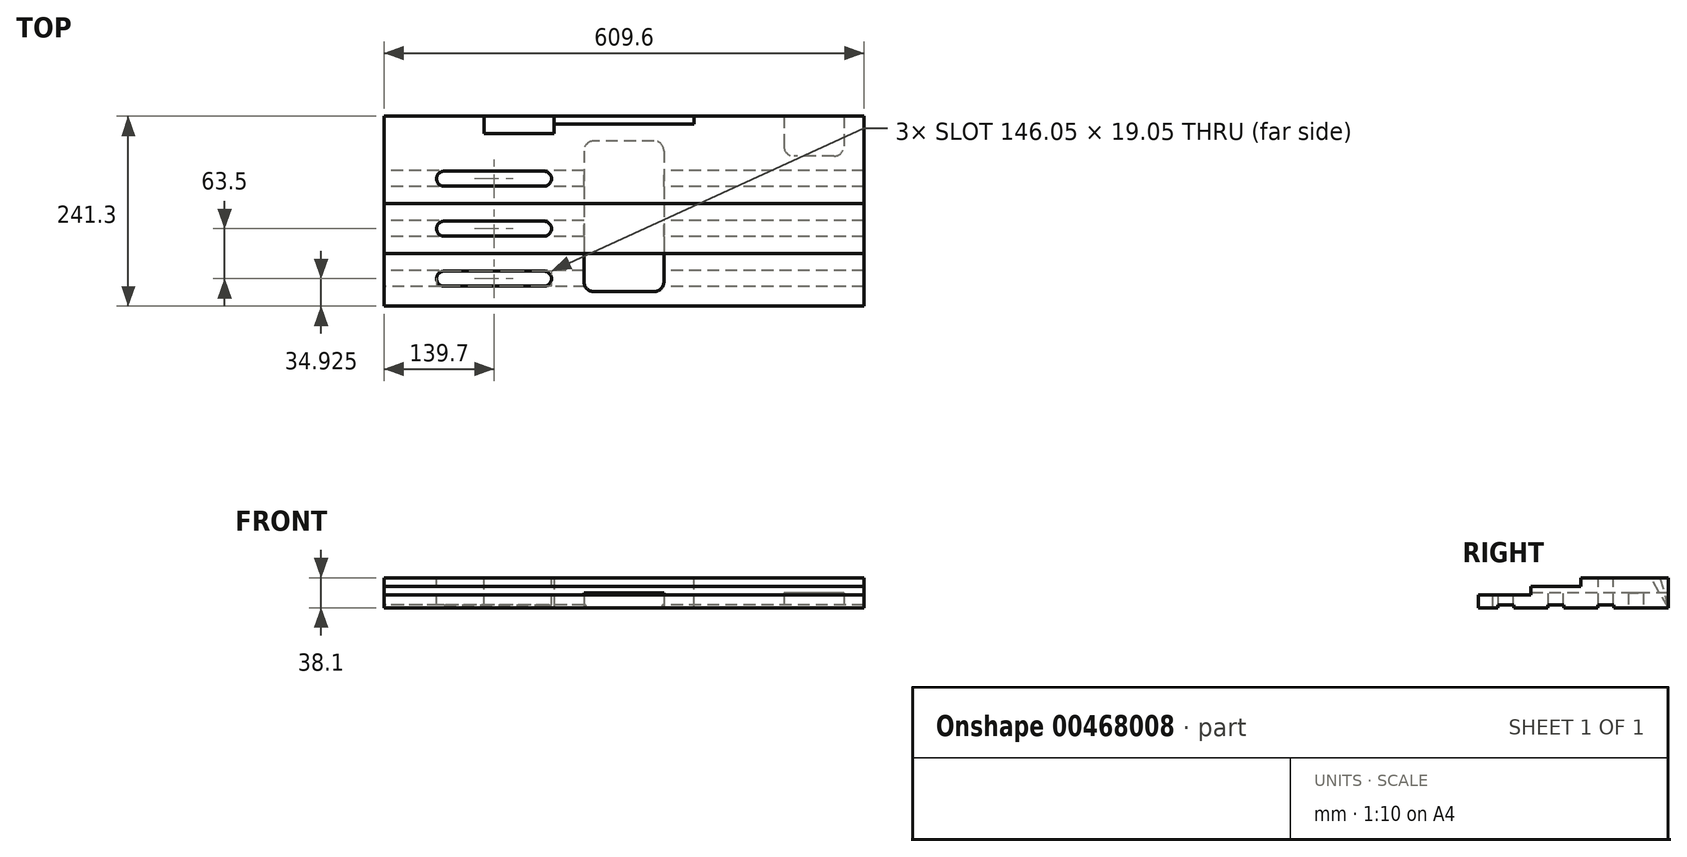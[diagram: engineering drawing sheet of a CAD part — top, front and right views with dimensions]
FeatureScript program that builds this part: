
annotation { "Feature Type Name" : "Feature", "Feature Type Description" : "" }
export const myFeature = defineFeature(function(context is Context, id is Id, definition is map)
    precondition{}
    {
        {
            var Q0;
            Q0=qCreatedBy(makeId("Top.planeOp"),FACE);
            var sketch = newSketch(context, id + "F0", { "sketchPlane" : qUnion([Q0])});
            skLineSegment(sketch, "E0.bottom", {"start": v(304.8, 120.65) * mm, "end": v(-304.8, 120.65) * mm});
            skLineSegment(sketch, "E0.top", {"start": v(304.8, -120.65) * mm, "end": v(-304.8, -120.65) * mm});
            skLineSegment(sketch, "E0.left", {"start": v(304.8, 120.65) * mm, "end": v(304.8, -120.65) * mm});
            skLineSegment(sketch, "E0.right", {"start": v(-304.8, 120.65) * mm, "end": v(-304.8, -120.65) * mm});
            skPoint(sketch, "E0.middle", {"position": v(0, 0) * mm});
            skSolve(sketch);
        }
        {
            var Q0;
            Q0 = qSketchRegion(id + "F0", true);
            extrude(context, id + "F1", {"entities" : qUnion([Q0]), "depth" : 38.1 * mm});
        }
        {
            var Q0;
            Q0=makeQuery(id+"F1.opExtrude","CAP_FACE",FACE,{"disambiguationData":[OSD([sQuery(id+"F0.wireOp",EDGE,"E0.bottom"),sQuery(id+"F0.wireOp",EDGE,"E0.top"),sQuery(id+"F0.wireOp",EDGE,"E0.left"),sQuery(id+"F0.wireOp",EDGE,"E0.right")])],"isStart":false});
            var sketch = newSketch(context, id + "F2", { "sketchPlane" : qUnion([Q0])});
            skLineSegment(sketch, "E1", {"start": v(-228.6, -85.73) * mm, "end": v(-101.6, -85.73) * mm});
            skArc(sketch, "E2.0.startCap", {"start": v(-228.6, -76.2) * mm, "mid": v(-238.12, -85.73) * mm, "end": v(-228.6, -95.25) * mm});
            skArc(sketch, "E2.0.endCap", {"start": v(-101.6, -95.25) * mm, "mid": v(-92.07, -85.72) * mm, "end": v(-101.6, -76.2) * mm});
            skLineSegment(sketch, "E2.0.left", {"start": v(-228.6, -95.25) * mm, "end": v(-101.6, -95.25) * mm});
            skLineSegment(sketch, "E2.0.right", {"start": v(-228.6, -76.2) * mm, "end": v(-101.6, -76.2) * mm});
            skArc(sketch, "E3.0.1.0", {"start": v(-101.6, -31.75) * mm, "mid": v(-92.07, -22.23) * mm, "end": v(-101.6, -12.7) * mm});
            skLineSegment(sketch, "E3.0.1.1", {"start": v(-228.6, -22.23) * mm, "end": v(-101.6, -22.23) * mm});
            skArc(sketch, "E3.0.1.2", {"start": v(-228.6, -12.7) * mm, "mid": v(-238.12, -22.22) * mm, "end": v(-228.6, -31.75) * mm});
            skLineSegment(sketch, "E3.0.1.3", {"start": v(-228.6, -31.75) * mm, "end": v(-101.6, -31.75) * mm});
            skLineSegment(sketch, "E3.0.1.4", {"start": v(-228.6, -12.7) * mm, "end": v(-101.6, -12.7) * mm});
            skArc(sketch, "E3.0.2.0", {"start": v(-101.6, 31.75) * mm, "mid": v(-92.07, 41.27) * mm, "end": v(-101.6, 50.8) * mm});
            skLineSegment(sketch, "E3.0.2.1", {"start": v(-228.6, 41.27) * mm, "end": v(-101.6, 41.27) * mm});
            skArc(sketch, "E3.0.2.2", {"start": v(-228.6, 50.8) * mm, "mid": v(-238.12, 41.27) * mm, "end": v(-228.6, 31.75) * mm});
            skLineSegment(sketch, "E3.0.2.3", {"start": v(-228.6, 31.75) * mm, "end": v(-101.6, 31.75) * mm});
            skLineSegment(sketch, "E3.0.2.4", {"start": v(-228.6, 50.8) * mm, "end": v(-101.6, 50.8) * mm});
            skLineSegment(sketch, "E3.direction1", {"start": v(-228.6, -95.25) * mm, "end": v(-203.2, -95.25) * mm, "construction": true});
            skLineSegment(sketch, "E3.direction2", {"start": v(-228.6, -95.25) * mm, "end": v(-228.6, -31.75) * mm, "construction": true});
            skSolve(sketch);
        }
        {
            var Q0;
            Q0 = qSketchRegion(id + "F2", true);
            extrude(context, id + "F3", {"entities" : qUnion([Q0]), "operationType" : NewBodyOperationType.REMOVE, "endBound" : BoundingType.THROUGH_ALL, "oppositeDirection" : true, "depth" : 31.75 * mm});
        }
        {
            var Q0;
            Q0=makeQuery(id+"F1.opExtrude","CAP_FACE",FACE,{"disambiguationData":[OSD([sQuery(id+"F0.wireOp",EDGE,"E0.bottom"),sQuery(id+"F0.wireOp",EDGE,"E0.top"),sQuery(id+"F0.wireOp",EDGE,"E0.left"),sQuery(id+"F0.wireOp",EDGE,"E0.right")])],"isStart":true});
            var sketch = newSketch(context, id + "F4", { "sketchPlane" : qUnion([Q0])});
            skLineSegment(sketch, "E4.bottom", {"start": v(279.4, -120.65) * mm, "end": v(203.2, -120.65) * mm});
            skLineSegment(sketch, "E4.top", {"start": v(279.4, -69.85) * mm, "end": v(203.2, -69.85) * mm});
            skLineSegment(sketch, "E4.left", {"start": v(279.4, -120.65) * mm, "end": v(279.4, -69.85) * mm});
            skLineSegment(sketch, "E4.right", {"start": v(203.2, -120.65) * mm, "end": v(203.2, -69.85) * mm});
            skSolve(sketch);
        }
        {
            var Q0;
            Q0 = qSketchRegion(id + "F4", true);
            extrude(context, id + "F5", {"entities" : qUnion([Q0]), "operationType" : NewBodyOperationType.REMOVE, "oppositeDirection" : true, "depth" : 19.05 * mm});
        }
        {
            var Q0;
            Q0=makeQuery(id+"F5.boolean.opBoolean","COPY",EDGE,{"derivedFrom":makeQuery(id+"F5.opExtrude","SWEPT_EDGE",EDGE,{"disambiguationData":[OSD([sQuery(id+"F4.wireOp",EDGE,"E4.top"),sQuery(id+"F4.wireOp",EDGE,"E4.left")])]})});
            var Q1;
            Q1=makeQuery(id+"F5.boolean.opBoolean","COPY",EDGE,{"derivedFrom":makeQuery(id+"F5.opExtrude","SWEPT_EDGE",EDGE,{"disambiguationData":[OSD([sQuery(id+"F4.wireOp",EDGE,"E4.top"),sQuery(id+"F4.wireOp",EDGE,"E4.right")])]})});
            fillet(context, id + "F6", {"entities" : qUnion([Q0, Q1]), "radius" : 12.7 * mm, "tangentPropagation" : true, "allowEdgeOverflow" : false});
        }
        {
            var Q0;
            Q0=qCreatedBy(makeId("Right.planeOp"),FACE);
            var sketch = newSketch(context, id + "F7", { "sketchPlane" : qUnion([Q0])});
            skLineSegment(sketch, "E5", {"start": v(110.44, 38.1) * mm, "end": v(120.65, 0) * mm});
            skLineSegment(sketch, "E6", {"start": v(120.65, 0) * mm, "end": v(120.65, 38.1) * mm});
            skLineSegment(sketch, "E7", {"start": v(120.65, 38.1) * mm, "end": v(110.44, 38.1) * mm});
            skSolve(sketch);
        }
        {
            var Q0;
            Q0 = qSketchRegion(id + "F7", true);
            extrude(context, id + "F8", {"entities" : qUnion([Q0]), "operationType" : NewBodyOperationType.REMOVE, "endBound" : BoundingType.SYMMETRIC, "depth" : 177.8 * mm});
        }
        {
            var Q0;
            Q0=makeQuery(id+"F8.boolean.opBoolean","COPY",FACE,{"derivedFrom":makeQuery(id+"F8.opExtrude","CAP_FACE",FACE,{"disambiguationData":[OSD([sQuery(id+"F7.wireOp",EDGE,"E5"),sQuery(id+"F7.wireOp",EDGE,"E6"),sQuery(id+"F7.wireOp",EDGE,"E7")])],"isStart":true})});
            var sketch = newSketch(context, id + "F9", { "sketchPlane" : qUnion([Q0])});
            skLineSegment(sketch, "E8", {"start": v(120.65, 0) * mm, "end": v(98.65, 38.1) * mm});
            skLineSegment(sketch, "E9", {"start": v(98.65, 38.1) * mm, "end": v(120.65, 38.1) * mm});
            skLineSegment(sketch, "E10", {"start": v(120.65, 38.1) * mm, "end": v(120.65, 0) * mm});
            skSolve(sketch);
        }
        {
            var Q0;
            Q0 = qSketchRegion(id + "F9", true);
            extrude(context, id + "F10", {"entities" : qUnion([Q0]), "operationType" : NewBodyOperationType.REMOVE, "oppositeDirection" : true, "depth" : 88.9 * mm});
        }
        {
            var Q0;
            Q0=makeQuery(id+"F1.opExtrude","CAP_FACE",FACE,{"disambiguationData":[OSD([sQuery(id+"F0.wireOp",EDGE,"E0.bottom"),sQuery(id+"F0.wireOp",EDGE,"E0.top"),sQuery(id+"F0.wireOp",EDGE,"E0.left"),sQuery(id+"F0.wireOp",EDGE,"E0.right")])],"isStart":false});
            var sketch = newSketch(context, id + "F11", { "sketchPlane" : qUnion([Q0])});
            skLineSegment(sketch, "E11.bottom", {"start": v(-304.8, -120.65) * mm, "end": v(304.8, -120.65) * mm});
            skLineSegment(sketch, "E11.top", {"start": v(-304.8, -53.97) * mm, "end": v(304.8, -53.97) * mm});
            skLineSegment(sketch, "E11.left", {"start": v(-304.8, -120.65) * mm, "end": v(-304.8, -53.97) * mm});
            skLineSegment(sketch, "E11.right", {"start": v(304.8, -120.65) * mm, "end": v(304.8, -53.97) * mm});
            skLineSegment(sketch, "E12", {"start": v(-165.1, -31.75) * mm, "end": v(-165.1, -76.2) * mm, "construction": true});
            skPoint(sketch, "E13", {"position": v(-165.1, -53.97) * mm});
            skSolve(sketch);
        }
        {
            var Q0;
            Q0 = qSketchRegion(id + "F11", true);
            extrude(context, id + "F12", {"entities" : qUnion([Q0]), "operationType" : NewBodyOperationType.REMOVE, "oppositeDirection" : true, "depth" : 19.05 * mm + 3.05 * mm});
        }
        {
            var Q0;
            Q0=makeQuery(id+"F1.opExtrude","CAP_FACE",FACE,{"disambiguationData":[OSD([sQuery(id+"F0.wireOp",EDGE,"E0.bottom"),sQuery(id+"F0.wireOp",EDGE,"E0.top"),sQuery(id+"F0.wireOp",EDGE,"E0.left"),sQuery(id+"F0.wireOp",EDGE,"E0.right")])],"isStart":false});
            var sketch = newSketch(context, id + "F13", { "sketchPlane" : qUnion([Q0])});
            skLineSegment(sketch, "E14.bottom", {"start": v(-304.8, -53.97) * mm, "end": v(304.8, -53.97) * mm});
            skLineSegment(sketch, "E14.top", {"start": v(-304.8, 9.52) * mm, "end": v(304.8, 9.52) * mm});
            skLineSegment(sketch, "E14.left", {"start": v(-304.8, -53.97) * mm, "end": v(-304.8, 9.52) * mm});
            skLineSegment(sketch, "E14.right", {"start": v(304.8, -53.97) * mm, "end": v(304.8, 9.52) * mm});
            skLineSegment(sketch, "E15", {"start": v(-165.1, 31.75) * mm, "end": v(-165.1, -12.7) * mm, "construction": true});
            skPoint(sketch, "E16", {"position": v(-165.1, 9.52) * mm});
            skSolve(sketch);
        }
        {
            var Q0;
            Q0 = qSketchRegion(id + "F13", true);
            extrude(context, id + "F14", {"entities" : qUnion([Q0]), "operationType" : NewBodyOperationType.REMOVE, "oppositeDirection" : true, "depth" : 11.05 * mm});
        }
        {
            var Q0;
            Q0=makeQuery(id+"F1.opExtrude","CAP_FACE",FACE,{"disambiguationData":[OSD([sQuery(id+"F0.wireOp",EDGE,"E0.bottom"),sQuery(id+"F0.wireOp",EDGE,"E0.top"),sQuery(id+"F0.wireOp",EDGE,"E0.left"),sQuery(id+"F0.wireOp",EDGE,"E0.right")])],"isStart":true});
            var sketch = newSketch(context, id + "F15", { "sketchPlane" : qUnion([Q0])});
            skLineSegment(sketch, "E17.bottom", {"start": v(50.8, -89.22) * mm, "end": v(-50.8, -89.22) * mm});
            skLineSegment(sketch, "E17.top", {"start": v(50.8, 102.3) * mm, "end": v(-50.8, 102.3) * mm});
            skLineSegment(sketch, "E17.left", {"start": v(50.8, -89.22) * mm, "end": v(50.8, 102.3) * mm});
            skLineSegment(sketch, "E17.right", {"start": v(-50.8, -89.22) * mm, "end": v(-50.8, 102.3) * mm});
            skLineSegment(sketch, "E18", {"start": v(0, 0) * mm, "end": v(0, 102.3) * mm, "construction": true});
            skSolve(sketch);
        }
        {
            var Q0;
            Q0 = qSketchRegion(id + "F15", true);
            extrude(context, id + "F16", {"entities" : qUnion([Q0]), "operationType" : NewBodyOperationType.REMOVE, "oppositeDirection" : true, "depth" : 19.05 * mm});
        }
        {
            var Q0;
            Q0=makeQuery(id+"F16.boolean.opBoolean","COPY",EDGE,{"derivedFrom":makeQuery(id+"F16.opExtrude","SWEPT_EDGE",EDGE,{"disambiguationData":[OSD([sQuery(id+"F15.wireOp",EDGE,"E17.bottom"),sQuery(id+"F15.wireOp",EDGE,"E17.right")])]})});
            var Q1;
            Q1=makeQuery(id+"F16.boolean.opBoolean","COPY",EDGE,{"derivedFrom":makeQuery(id+"F16.opExtrude","SWEPT_EDGE",EDGE,{"disambiguationData":[OSD([sQuery(id+"F15.wireOp",EDGE,"E17.top"),sQuery(id+"F15.wireOp",EDGE,"E17.right")])]})});
            var Q2;
            Q2=makeQuery(id+"F16.boolean.opBoolean","COPY",EDGE,{"derivedFrom":makeQuery(id+"F16.opExtrude","SWEPT_EDGE",EDGE,{"disambiguationData":[OSD([sQuery(id+"F15.wireOp",EDGE,"E17.top"),sQuery(id+"F15.wireOp",EDGE,"E17.left")])]})});
            var Q3;
            Q3=makeQuery(id+"F16.boolean.opBoolean","COPY",EDGE,{"derivedFrom":makeQuery(id+"F16.opExtrude","SWEPT_EDGE",EDGE,{"disambiguationData":[OSD([sQuery(id+"F15.wireOp",EDGE,"E17.bottom"),sQuery(id+"F15.wireOp",EDGE,"E17.left")])]})});
            fillet(context, id + "F17", {"entities" : qUnion([Q0, Q1, Q2, Q3]), "radius" : 12.7 * mm, "tangentPropagation" : true, "allowEdgeOverflow" : false});
        }
        {
            var Q0;
            Q0=makeQuery(id+"F1.opExtrude","SWEPT_FACE",FACE,{"disambiguationData":[OSD([sQuery(id+"F0.wireOp",EDGE,"E0.right")])]});
            var sketch = newSketch(context, id + "F18", { "sketchPlane" : qUnion([Q0])});
            skLineSegment(sketch, "E19.bottom", {"start": v(-51.44, 0) * mm, "end": v(-31.11, 0) * mm});
            skLineSegment(sketch, "E19.top", {"start": v(-51.44, 3.3) * mm, "end": v(-31.11, 3.3) * mm});
            skLineSegment(sketch, "E19.left", {"start": v(-51.44, 0) * mm, "end": v(-51.44, 3.3) * mm});
            skLineSegment(sketch, "E19.right", {"start": v(-31.11, 0) * mm, "end": v(-31.11, 3.3) * mm});
            skPoint(sketch, "E19.middle", {"position": v(-41.27, 1.65) * mm});
            skLineSegment(sketch, "E20.bottom", {"start": v(12.06, 0) * mm, "end": v(32.38, 0) * mm});
            skLineSegment(sketch, "E20.top", {"start": v(12.06, 3.3) * mm, "end": v(32.38, 3.3) * mm});
            skLineSegment(sketch, "E20.left", {"start": v(12.06, 0) * mm, "end": v(12.06, 3.3) * mm});
            skLineSegment(sketch, "E20.right", {"start": v(32.38, 0) * mm, "end": v(32.38, 3.3) * mm});
            skPoint(sketch, "E20.middle", {"position": v(22.22, 1.65) * mm});
            skLineSegment(sketch, "E21.bottom", {"start": v(75.56, 0) * mm, "end": v(95.88, 0) * mm});
            skLineSegment(sketch, "E21.top", {"start": v(75.56, 3.3) * mm, "end": v(95.88, 3.3) * mm});
            skLineSegment(sketch, "E21.left", {"start": v(75.56, 0) * mm, "end": v(75.56, 3.3) * mm});
            skLineSegment(sketch, "E21.right", {"start": v(95.88, 0) * mm, "end": v(95.88, 3.3) * mm});
            skPoint(sketch, "E21.middle", {"position": v(85.72, 1.65) * mm});
            skSolve(sketch);
        }
        {
            var Q0;
            Q0 = qSketchRegion(id + "F18", true);
            extrude(context, id + "F19", {"entities" : qUnion([Q0]), "operationType" : NewBodyOperationType.REMOVE, "endBound" : BoundingType.THROUGH_ALL, "oppositeDirection" : true, "depth" : 254 * mm});
        }
    });
